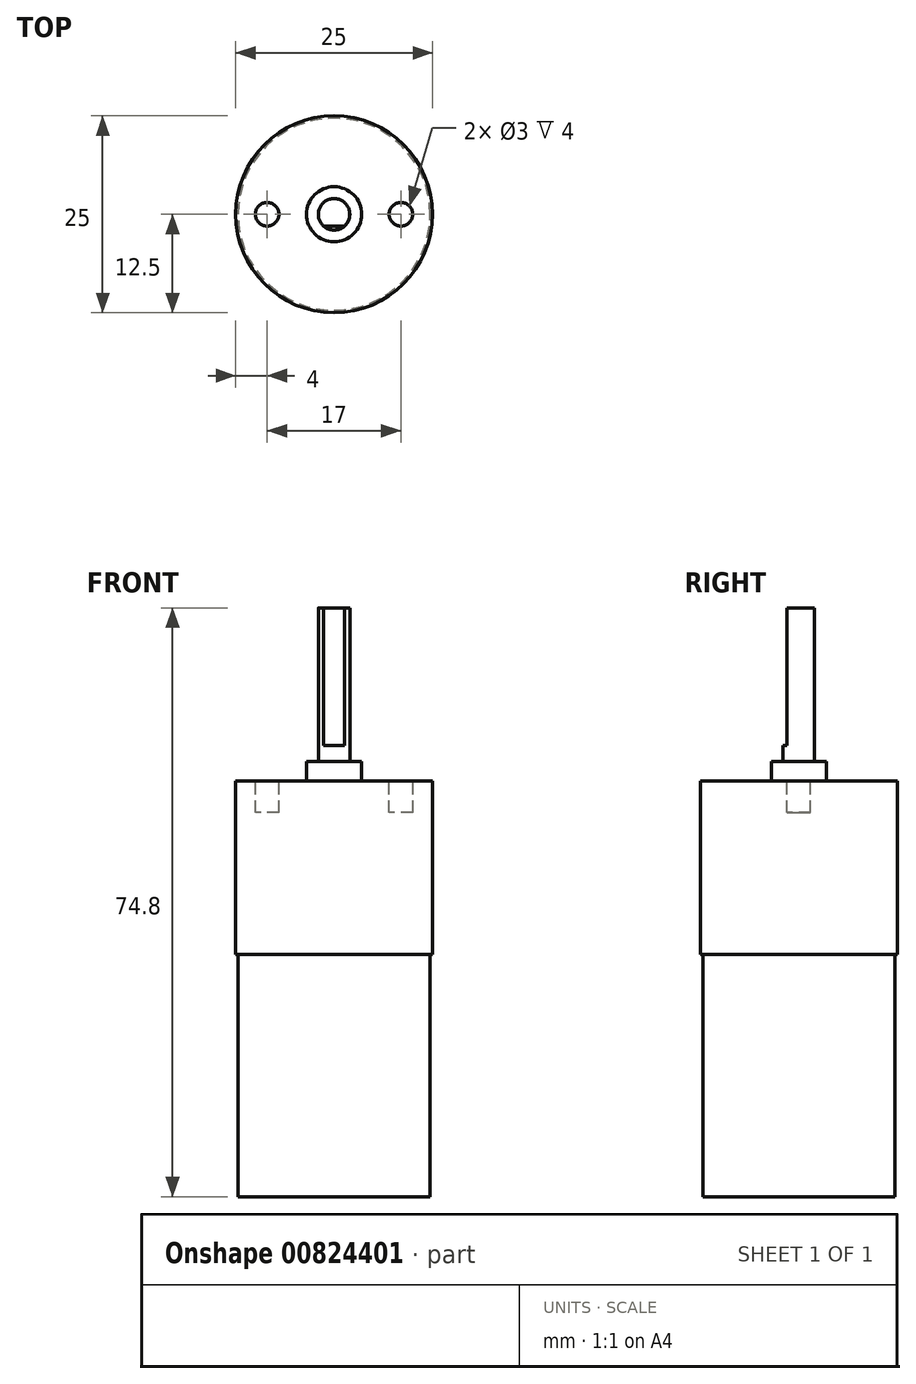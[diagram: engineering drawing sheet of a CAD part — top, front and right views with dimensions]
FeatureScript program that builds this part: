
annotation { "Feature Type Name" : "Feature", "Feature Type Description" : "" }
export const myFeature = defineFeature(function(context is Context, id is Id, definition is map)
    precondition{}
    {
        {
            var Q0;
            Q0=qCreatedBy(makeId("Top.planeOp"),FACE);
            var sketch = newSketch(context, id + "F0", { "sketchPlane" : qUnion([Q0])});
            skCircle(sketch, "E0", {"center": v(0, 0) * mm, "radius": 12.5 * mm});
            skSolve(sketch);
        }
        {
            var Q0;
            Q0=makeQuery(id+"F0.imprint","IMPRINT",FACE,{"disambiguationData":[TD([[makeQuery(id+"F0.imprint","IMPRINT",EDGE,{"derivedFrom":sQuery(id+"F0.wireOp",EDGE,"E0")}),1.0]])]});
            extrude(context, id + "F1", {"entities" : qUnion([Q0]), "oppositeDirection" : true, "depth" : 22 * mm, "offsetDistance" : 25 * mm});
        }
        {
            var Q0;
            Q0=makeQuery(id+"F1.opExtrude","CAP_FACE",FACE,{"disambiguationData":[OSD([sQuery(id+"F0.wireOp",EDGE,"E0")])],"isStart":false});
            var sketch = newSketch(context, id + "F2", { "sketchPlane" : qUnion([Q0])});
            skCircle(sketch, "E1", {"center": v(0, 0) * mm, "radius": 12.2 * mm});
            skSolve(sketch);
        }
        {
            var Q0;
            Q0=makeQuery(id+"F2.imprint","IMPRINT",FACE,{"disambiguationData":[TD([[makeQuery(id+"F2.imprint","IMPRINT",EDGE,{"derivedFrom":sQuery(id+"F2.wireOp",EDGE,"E1")}),1.0]])]});
            extrude(context, id + "F3", {"entities" : qUnion([Q0]), "operationType" : NewBodyOperationType.ADD, "depth" : 30.8 * mm, "offsetDistance" : 25 * mm});
        }
        {
            var Q0;
            Q0=makeQuery(id+"F1.opExtrude","CAP_FACE",FACE,{"disambiguationData":[OSD([sQuery(id+"F0.wireOp",EDGE,"E0")])],"isStart":true});
            var sketch = newSketch(context, id + "F4", { "sketchPlane" : qUnion([Q0])});
            skCircle(sketch, "E2", {"center": v(0, 0) * mm, "radius": 3.5 * mm});
            skSolve(sketch);
        }
        {
            var Q0;
            Q0=makeQuery(id+"F4.imprint","IMPRINT",FACE,{"disambiguationData":[TD([[makeQuery(id+"F4.imprint","IMPRINT",EDGE,{"derivedFrom":sQuery(id+"F4.wireOp",EDGE,"E2")}),1.0]])]});
            extrude(context, id + "F5", {"entities" : qUnion([Q0]), "operationType" : NewBodyOperationType.ADD, "depth" : 2.5 * mm, "offsetDistance" : 25 * mm});
        }
        {
            var Q0;
            Q0=makeQuery(id+"F1.opExtrude","CAP_FACE",FACE,{"disambiguationData":[OSD([sQuery(id+"F0.wireOp",EDGE,"E0")])],"isStart":true});
            var sketch = newSketch(context, id + "F6", { "sketchPlane" : qUnion([Q0])});
            skCircle(sketch, "E3", {"center": v(0, 0) * mm, "radius": 2 * mm});
            skSolve(sketch);
        }
        {
            var Q0;
            Q0 = qSketchRegion(id + "F6", true);
            extrude(context, id + "F7", {"entities" : qUnion([Q0]), "operationType" : NewBodyOperationType.ADD, "depth" : 22 * mm, "offsetDistance" : 25 * mm});
        }
        {
            var Q0;
            Q0=makeQuery(id+"F7.opExtrude","CAP_FACE",FACE,{"disambiguationData":[OSD([sQuery(id+"F6.wireOp",EDGE,"E3")])],"isStart":false});
            var sketch = newSketch(context, id + "F8", { "sketchPlane" : qUnion([Q0])});
            skCircle(sketch, "E4.0.0", {"center": v(0, 0) * mm, "radius": 2 * mm});
            skLineSegment(sketch, "E5", {"start": v(-1.32, -1.5) * mm, "end": v(1.32, -1.5) * mm});
            skSolve(sketch);
        }
        {
            var Q0;
            {var subQ0=sQuery(id+"F8.wireOp",EDGE,"E5");Q0=makeQuery(id+"F8.imprint","IMPRINT",FACE,{"disambiguationData":[TD([[makeQuery(id+"F8.imprint","IMPRINT",EDGE,{"derivedFrom":subQ0}),-1.0]])]});}
            extrude(context, id + "F9", {"entities" : qUnion([Q0]), "operationType" : NewBodyOperationType.REMOVE, "oppositeDirection" : true, "depth" : 17.5 * mm, "offsetDistance" : 25 * mm});
        }
        {
            var Q0;
            Q0=makeQuery(id+"F1.opExtrude","CAP_FACE",FACE,{"disambiguationData":[OSD([sQuery(id+"F0.wireOp",EDGE,"E0")])],"isStart":true});
            var sketch = newSketch(context, id + "F10", { "sketchPlane" : qUnion([Q0])});
            skCircle(sketch, "E6", {"center": v(-8.5, 0) * mm, "radius": 1.5 * mm});
            skCircle(sketch, "E7", {"center": v(8.5, 0) * mm, "radius": 1.5 * mm});
            skLineSegment(sketch, "E8", {"start": v(-8.5, 0) * mm, "end": v(0, 0) * mm, "construction": true});
            skLineSegment(sketch, "E9", {"start": v(0, 0) * mm, "end": v(8.5, 0) * mm, "construction": true});
            skSolve(sketch);
        }
        {
            var Q0;
            Q0=makeQuery(id+"F10.imprint","IMPRINT",FACE,{"disambiguationData":[TD([[makeQuery(id+"F10.imprint","IMPRINT",EDGE,{"derivedFrom":sQuery(id+"F10.wireOp",EDGE,"E6")}),1.0]])]});
            var Q1;
            Q1=makeQuery(id+"F10.imprint","IMPRINT",FACE,{"disambiguationData":[TD([[makeQuery(id+"F10.imprint","IMPRINT",EDGE,{"derivedFrom":sQuery(id+"F10.wireOp",EDGE,"E7")}),1.0]])]});
            extrude(context, id + "F11", {"entities" : qUnion([Q0, Q1]), "operationType" : NewBodyOperationType.REMOVE, "oppositeDirection" : true, "depth" : 4 * mm, "offsetDistance" : 25 * mm});
        }
    });
